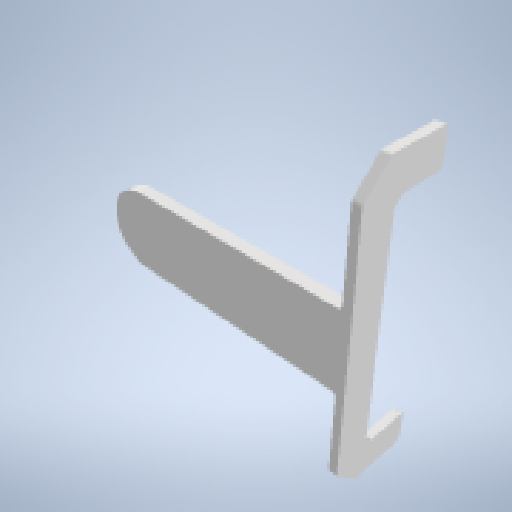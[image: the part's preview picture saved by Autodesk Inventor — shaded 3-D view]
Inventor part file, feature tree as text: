
AUTODESK INVENTOR PART (.ipt)
format: ipt  version: 2023 (Build 270158000, 158)  size: 312,832 bytes
history: native  units: in
note: dims shown in document units (in); Inventor stores cm internally (conversion verified against a paired STEP export)
features: sketch x6, extrude x5, fillet x3, chamfer x2, revolve x1
ambient origin geometry x8: Origin, YZ Plane, XZ Plane, XY Plane, X Axis, Y Axis, Z Axis, Center Point
bodies: Solid1 (feature_tree)
feature tree (17):
  extrude  "Extrusion1"  Depth=0.7087in
  extrude  "Extrusion2"  Depth=0.3543in
  revolve  "Revolution1"  [1 undecoded]
  extrude  "Extrusion3"  Depth=0.3543in
  fillet  "Fillet1"  Radius=2.7559in
  extrude  "Extrusion4"  Depth=0.0787in TaperAngle=0.0deg
  chamfer  "Chamfer1"  Distance=0.315in
  chamfer  "Chamfer2"  Distance=0.315in
  fillet  "Fillet3"  Radius=0.315in
  fillet  "Fillet4"  Radius=0.7874in
  extrude  "Extrusion5"  Depth=0.2362in TaperAngle=45.0deg
  sketch  "Sketch1"  dims[d0=0.7087in d1=2.3622in]
  sketch  "Sketch2"  dims[d2=0.1181in d3=0.0in d4=0.3543in]
  sketch  "Sketch4"  dims[d5=0.1969in d6=0.0in d7=0.1374in]
  sketch  "Sketch5"  dims[d8=0.0787in d9=0.0in d10=0.3543in d11=2.7559in]
  sketch  "Sketch6"  dims[d12=0.0in d13=0.0787in d14=0.0in]
  sketch  "Sketch7"  dims[d15=0.7874in d16=0.315in d17=0.315in d18=0.315in d19=0.7874in d21=0.2362in d22=0.0787in d23=45.0deg d24=0.0787in d25=0.0787in d26=45.0deg d27=0.0394in d28=0.0394in d29=0.4724in d30=0.0394in d31=0.0in]
note: 1 required parameter value undecoded (feature->parameter linkage not recoverable at this tier; creation-order binding heuristic only, values carry confidence <= 0.55)
